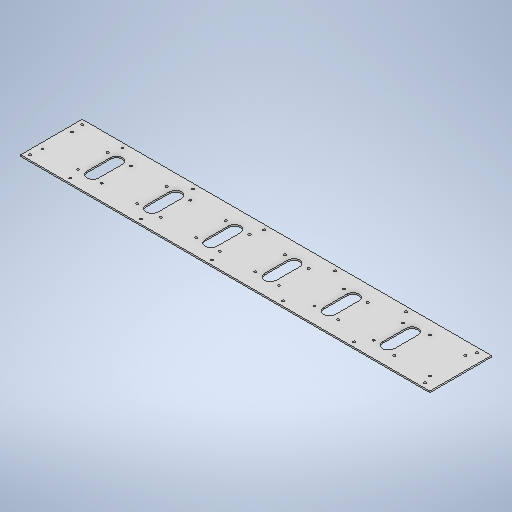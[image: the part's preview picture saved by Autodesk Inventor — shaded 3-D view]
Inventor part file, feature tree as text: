
AUTODESK INVENTOR PART (.ipt)
format: ipt  version: 2025.1 (Build 291241000, 241)  size: 397,312 bytes
history: native  units: in
note: dims shown in document units (in); Inventor stores cm internally (conversion verified against a paired STEP export)
features: extrude x1, sketch x1
ambient origin geometry x8: Origin, YZ Plane, XZ Plane, XY Plane, X Axis, Y Axis, Z Axis, Center Point
bodies: Solid1 (feature_tree)
feature tree (2):
  extrude  "Extrusion1"  Depth=0.125in
  sketch  "Sketch1"  dims[d8=34.6in d9=2.6in d10=0.8in d11=90.0deg d12=34.6in d14=0.8in d15=0.0in d16=0.2in d17=6.0in d19=0.2in d20=6.0in d21=0.2in d22=6.0in d23=0.2in d24=6.0in d25=0.2in d26=6.0in d27=0.2in d28=0.4in d29=90.0deg d30=0.4in d31=90.0deg d32=0.2in d33=1.1in d34=90.0deg d35=1.1in d36=90.0deg d37=0.2in d38=3.0in d39=0.0in d40=0.2in d41=1.0in d43=1.0in d46=0.5in d47=90.0deg d48=0.5in d51=0.5in d52=0.0in d53=1.25in d54=90.0deg d55=0.2in d56=3.0in d57=0.0in d58=0.2in d59=2.0in d60=180.0deg d61=1.0in d62=0.2in d63=3.0in d64=0.2in d65=2.0in d66=1.0in d67=0.2in d68=3.0in d69=0.2in d70=2.0in d71=1.0in d72=0.2in d73=3.0in d74=0.2in d75=2.0in d76=1.0in d77=0.2in d78=3.0in d79=0.2in d80=2.0in d81=1.0in d82=0.2in d83=3.0in d84=0.2in d85=2.0in d86=0.125in d87=0.0in]
